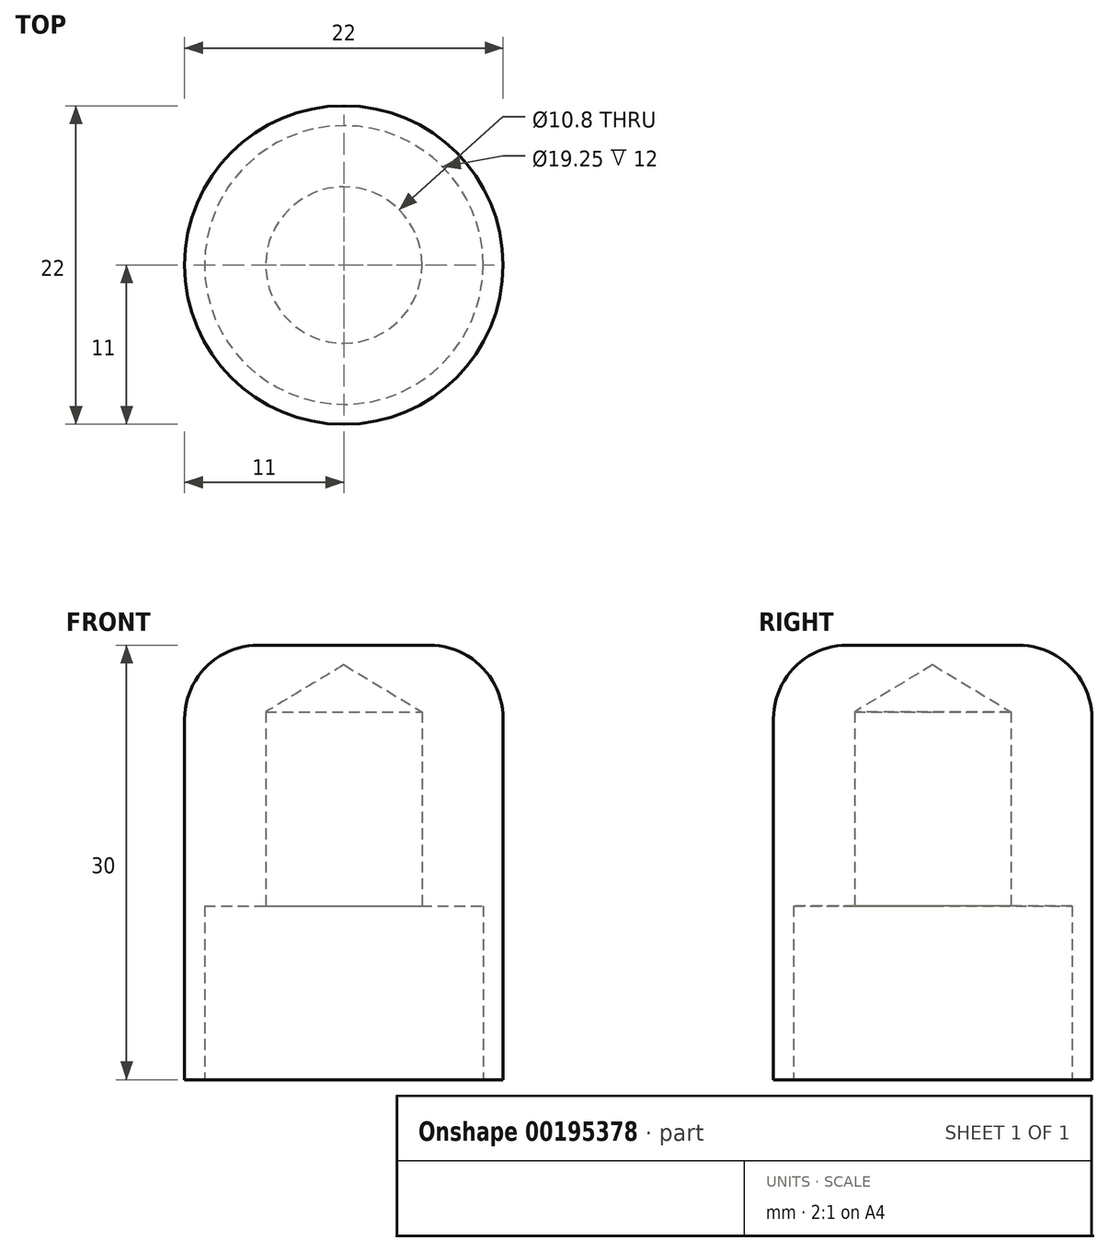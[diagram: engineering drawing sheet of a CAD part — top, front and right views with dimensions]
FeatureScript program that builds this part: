
annotation { "Feature Type Name" : "Feature", "Feature Type Description" : "" }
export const myFeature = defineFeature(function(context is Context, id is Id, definition is map)
    precondition{}
    {
        {
            var Q0;
            Q0=qCreatedBy(makeId("Top.planeOp"),FACE);
            var sketch = newSketch(context, id + "F0", { "sketchPlane" : qUnion([Q0])});
            skCircle(sketch, "E0", {"center": v(0, 0) * mm, "radius": 11 * mm});
            skSolve(sketch);
        }
        {
            var Q0;
            Q0 = qSketchRegion(id + "F0", true);
            extrude(context, id + "F1", {"entities" : qUnion([Q0]), "depth" : 30 * mm});
        }
        {
            var Q0;
            Q0=sQuery(id+"F0.wireOp",VERTEX,"E0.center");
            var Q1;
            Q1=makeQuery(id+"F1.opExtrude","SWEPT_BODY",BODY,{"disambiguationData":[OSD([sQuery(id+"F0.wireOp",EDGE,"E0")])]});
            hole(context, id + "F2", {"style" : HoleStyle.C_BORE, "endStyle" : HoleEndStyle.BLIND, "oppositeDirection" : true, "standardTappedOrClearance" : lookupTablePath({ "standard" : "ISO", "engagement" : "75%", "pitch" : "1.25 mm", "size" : "M12", "type" : "Tapped" }), "standardBlindInLast" : lookupTablePath({ "standard" : "ISO", "engagement" : "75%", "pitch" : "1.25 mm", "size" : "M12", "type" : "Tapped" }), "holeDiameter" : 10.8 * mm, "cBoreDiameter" : 19.25 * mm, "cBoreDepth" : 12 * mm, "holeDepth" : 25.4 * mm, "locations" : qUnion([Q0]), "scope" : qUnion([Q1]), "majorDiameter" : 12 * mm});
        }
        {
            var Q0;
            Q0=makeQuery(id+"F1.opExtrude","CAP_EDGE",EDGE,{"disambiguationData":[OSD([sQuery(id+"F0.wireOp",EDGE,"E0")])],"isStart":false});
            fillet(context, id + "F3", {"entities" : qUnion([Q0]), "radius" : 5.08 * mm, "tangentPropagation" : true, "allowEdgeOverflow" : false});
        }
    });
